FCSTD DOCUMENT  (FreeCAD 0.19R)
Label: drone
License: All rights reserved
LicenseURL: http://en.wikipedia.org/wiki/All_rights_reserved
objects: PartDesign::Body×1, Sketcher::SketchObject×1, App::Part×1
note: 2 computed .brp shape members not serialized (recipe doc carries the construction recipe); baked Part::Feature solids carry a one-line shape summary decoded from their .brp

FEATURE [PartDesign::Body] Body  label="controller_plate"
  Origin = -> Origin
FEATURE [Sketcher::SketchObject] Sketch  label="main_sketch"
  FullyConstrained = true
  MapMode = 5
  Support = -> [XY_Plane001]
  sketch-geometry (4):
    g0: LineSegment StartX=-15 StartY=15 StartZ=0 EndX=15 EndY=15 EndZ=0
    g1: LineSegment StartX=15 StartY=15 StartZ=0 EndX=15 EndY=-15 EndZ=0
    g2: LineSegment StartX=15 StartY=-15 StartZ=0 EndX=-15 EndY=-15 EndZ=0
    g3: LineSegment StartX=-15 StartY=-15 StartZ=0 EndX=-15 EndY=15 EndZ=0
  constraints (11):
    c: Coincident(g0,g1)
    c: Coincident(g1,g2)
    c: Coincident(g2,g3)
    c: Coincident(g3,g0)
    c: Horizontal(g0)
    c: Horizontal(g2)
    c: Vertical(g1)
    c: Vertical(g3)
    c: Symmetric(g0,g1,g-1)
    c: Equal(g1,g0)
    c: DistanceY(g1,g1) = 30
FEATURE [App::Part] Part  label="drone"
  Group = -> [Body,Sketch]
  Origin = -> Origin001
